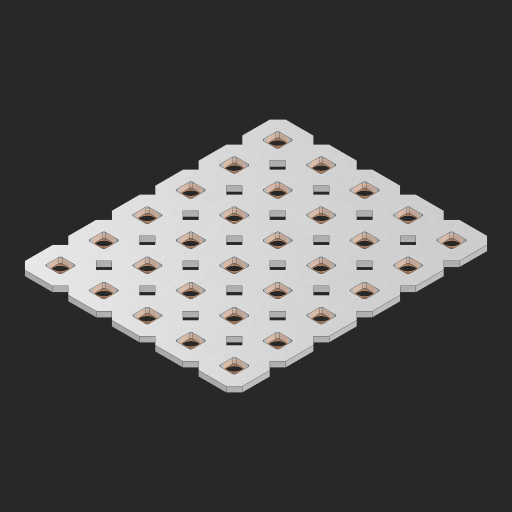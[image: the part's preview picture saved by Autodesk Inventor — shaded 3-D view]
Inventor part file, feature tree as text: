
AUTODESK INVENTOR PART (.ipt)
format: ipt  version: 2023 (Build 270158000, 158)  size: 648,192 bytes
history: native  units: in
note: dims shown in document units (in); Inventor stores cm internally (conversion verified against a paired STEP export)
features: other x31, extrude x29, sketch x2, pattern_linear x1
ambient origin geometry x8: Origin, YZ Plane, XZ Plane, XY Plane, X Axis, Y Axis, Z Axis, Center Point
bodies: Solid1 (feature_tree), Body (feature_tree)
feature tree (63):
  pattern_linear  "Rectangular Pattern1"  Spacing1=0.09in  [1 undecoded]
  sketch  "Sketch1"  dims[d1=0.5in]
  sketch  "Sketch2"  dims[d2=0.182in d3=0.09in d4=0.09in d5=0.09in d6=0.09in d7=0.09in d8=0.09in d9=0.09in d10=0.09in d11=0.02in d13=0.0in d14=0.172in d15=0.0625in d16=0.0in d19=0.5in d22=0.5in]
  other  "Srf1"
  other  "Srf126"
  other  "Srf127"
  other  "Srf128"
  other  "Srf129"
  other  "Srf130"
  other  "Srf268"
  other  "Srf269"
  other  "Srf270"
  other  "Srf271"
  other  "Srf272"
  other  "Srf273"
  other  "Srf293"
  other  "Srf294"
  other  "Srf295"
  other  "Srf296"
  other  "Srf297"
  other  "Srf298"
  other  "Srf318"
  other  "Srf319"
  other  "Srf320"
  other  "Srf321"
  other  "Srf322"
  other  "Srf323"
  other  "Srf343"
  other  "Srf344"
  other  "Srf345"
  other  "Srf346"
  other  "Srf347"
  other  "Srf348"
  other  "Circle"
  extrude  "ExtrusionSrf126"  Depth=0.09in
  extrude  "ExtrusionSrf127"  Depth=0.09in
  extrude  "ExtrusionSrf128"  Depth=0.09in
  extrude  "ExtrusionSrf129"  Depth=0.09in
  extrude  "ExtrusionSrf130"  Depth=0.09in
  extrude  "ExtrusionSrf268"  Depth=0.09in
  extrude  "ExtrusionSrf269"  Depth=0.09in
  extrude  "ExtrusionSrf270"  Depth=0.02in
  extrude  "ExtrusionSrf271"  TaperAngle=0.0deg  [1 undecoded]
  extrude  "ExtrusionSrf272"  Depth=0.5in
  extrude  "ExtrusionSrf273"  Depth=0.0625in TaperAngle=0.0deg
  extrude  "ExtrusionSrf293"  Depth=0.5in
  extrude  "ExtrusionSrf294"  Depth=0.5in
  extrude  "ExtrusionSrf295"  [1 undecoded]
  extrude  "ExtrusionSrf296"  [1 undecoded]
  extrude  "ExtrusionSrf297"  [1 undecoded]
  extrude  "ExtrusionSrf298"  [1 undecoded]
  extrude  "ExtrusionSrf318"  [1 undecoded]
  extrude  "ExtrusionSrf319"  [1 undecoded]
  extrude  "ExtrusionSrf320"  [1 undecoded]
  extrude  "ExtrusionSrf321"  [1 undecoded]
  extrude  "ExtrusionSrf322"  [1 undecoded]
  extrude  "ExtrusionSrf323"  [1 undecoded]
  extrude  "ExtrusionSrf343"  [1 undecoded]
  extrude  "ExtrusionSrf344"  [1 undecoded]
  extrude  "ExtrusionSrf345"  [1 undecoded]
  extrude  "ExtrusionSrf346"  [1 undecoded]
  extrude  "ExtrusionSrf347"  [1 undecoded]
  extrude  "ExtrusionSrf348"  [1 undecoded]
note: 18 required parameter values undecoded (feature->parameter linkage not recoverable at this tier; creation-order binding heuristic only, values carry confidence <= 0.55)
